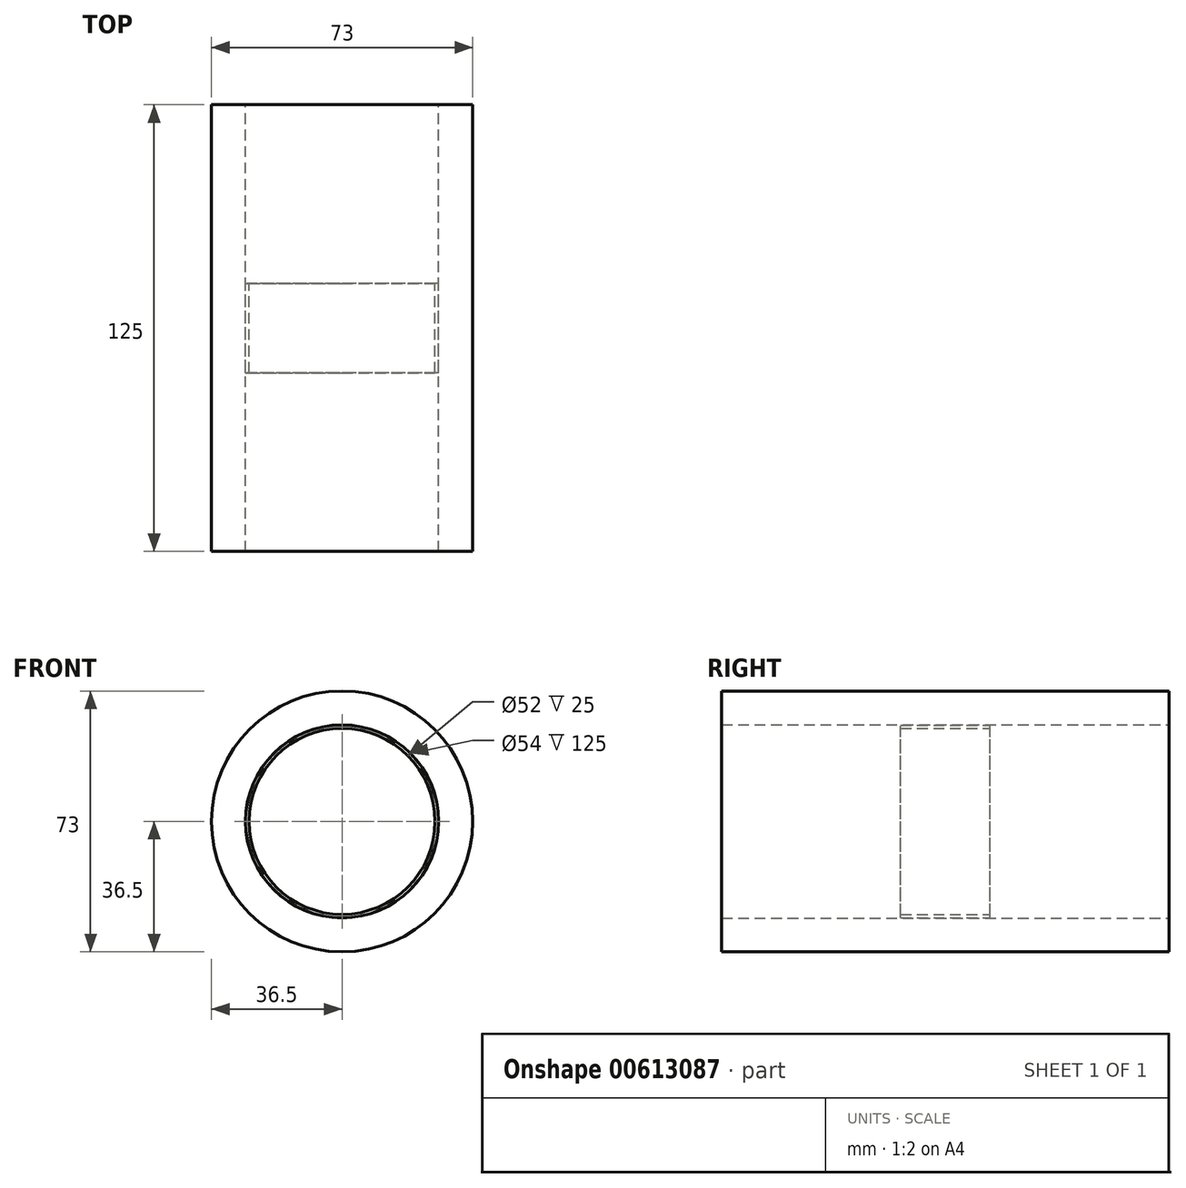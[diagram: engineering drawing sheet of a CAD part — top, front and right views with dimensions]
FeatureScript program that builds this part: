
annotation { "Feature Type Name" : "Feature", "Feature Type Description" : "" }
export const myFeature = defineFeature(function(context is Context, id is Id, definition is map)
    precondition{}
    {
        {
            var Q0;
            Q0=qCreatedBy(makeId("Front.planeOp"),FACE);
            var sketch = newSketch(context, id + "F0", { "sketchPlane" : qUnion([Q0])});
            skCircle(sketch, "E0", {"center": v(0, 0) * mm, "radius": 36.5 * mm});
            skCircle(sketch, "E1", {"center": v(0, 0) * mm, "radius": 27 * mm});
            skSolve(sketch);
        }
        {
            var Q0;
            Q0=makeQuery(id+"F0.imprint","IMPRINT",FACE,{"disambiguationData":[TD([[makeQuery(id+"F0.imprint","IMPRINT",EDGE,{"derivedFrom":sQuery(id+"F0.wireOp",EDGE,"E0")}),1.0]])]});
            extrude(context, id + "F1", {"entities" : qUnion([Q0]), "depth" : 62.5 * mm, "offsetDistance" : 25 * mm, "hasSecondDirection" : true, "secondDirectionOppositeDirection" : true, "secondDirectionDepth" : 62.5 * mm});
        }
        {
            var Q0;
            Q0=qCreatedBy(makeId("Front.planeOp"),FACE);
            var sketch = newSketch(context, id + "F2", { "sketchPlane" : qUnion([Q0])});
            skCircle(sketch, "E2", {"center": v(0, 0) * mm, "radius": 26.95 * mm});
            skCircle(sketch, "E3", {"center": v(0, 0) * mm, "radius": 26 * mm});
            skSolve(sketch);
        }
        {
            var Q0;
            Q0=makeQuery(id+"F2.imprint","IMPRINT",FACE,{"disambiguationData":[TD([[makeQuery(id+"F2.imprint","IMPRINT",EDGE,{"derivedFrom":sQuery(id+"F2.wireOp",EDGE,"E2")}),1.0]])]});
            var Q1;
            Q1=sQuery(id+"F2.wireOp",EDGE,"E2");
            var Q2;
            Q2=sQuery(id+"F2.wireOp",EDGE,"E3");
            extrude(context, id + "F3", {"entities" : qUnion([Q0]), "surfaceEntities" : qUnion([Q1, Q2]), "depth" : 12.5 * mm, "offsetDistance" : 25 * mm, "hasSecondDirection" : true, "secondDirectionOppositeDirection" : true, "secondDirectionDepth" : 12.5 * mm});
        }
    });
